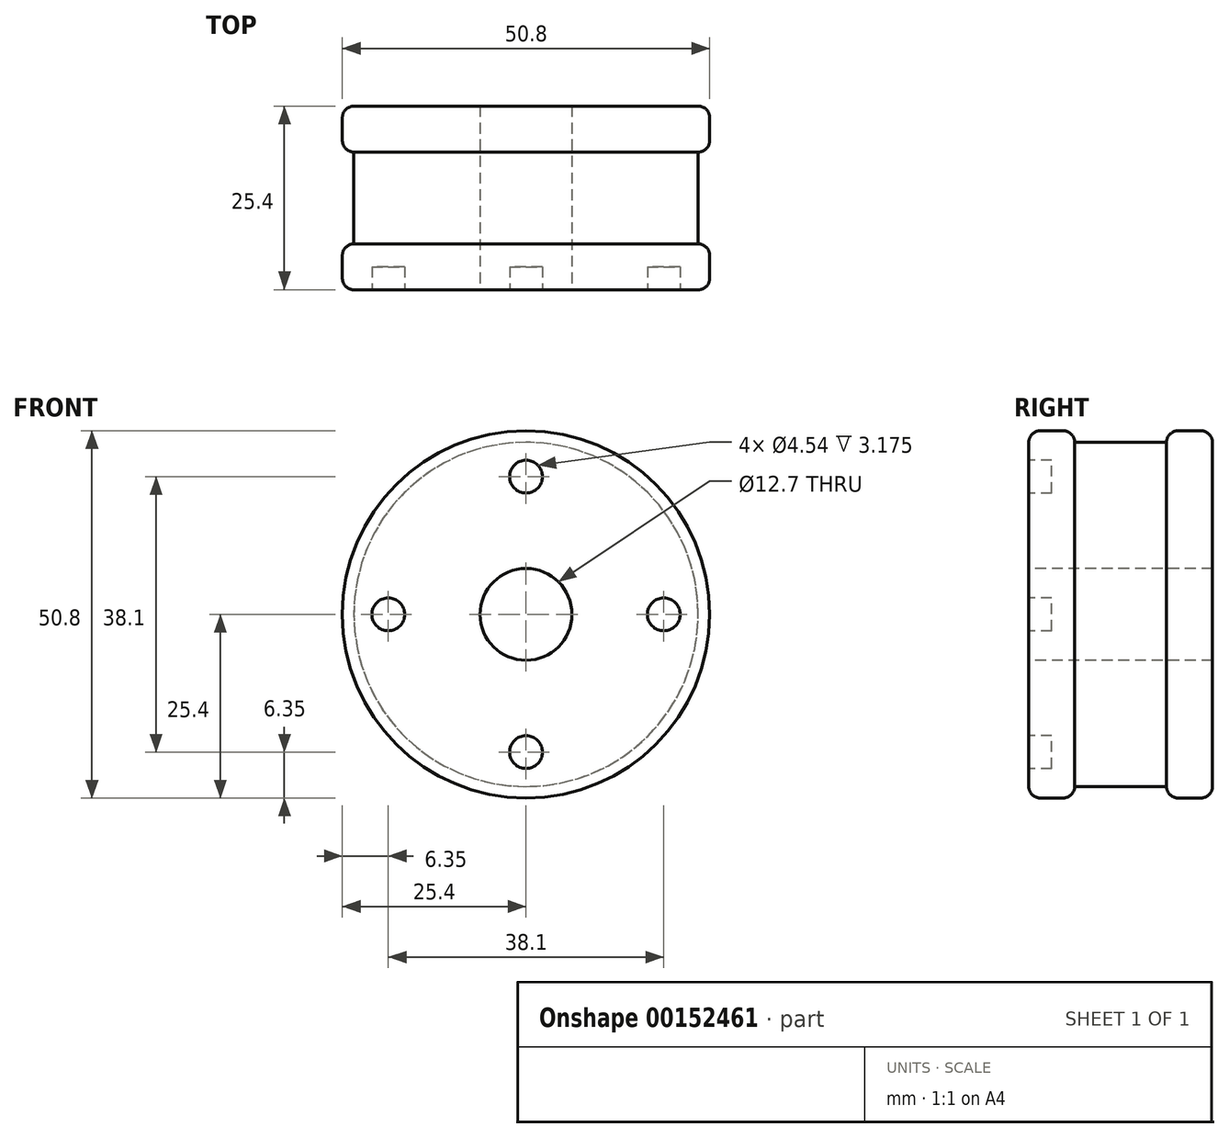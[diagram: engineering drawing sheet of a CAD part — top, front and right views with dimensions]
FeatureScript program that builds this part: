
annotation { "Feature Type Name" : "Feature", "Feature Type Description" : "" }
export const myFeature = defineFeature(function(context is Context, id is Id, definition is map)
    precondition{}
    {
        {
            var Q0;
            Q0=qCreatedBy(makeId("Front.planeOp"),FACE);
            var sketch = newSketch(context, id + "F0", { "sketchPlane" : qUnion([Q0])});
            skCircle(sketch, "E0", {"center": v(0, 0) * mm, "radius": 25.4 * mm});
            skSolve(sketch);
        }
        {
            var Q0;
            Q0 = qSketchRegion(id + "F0", true);
            extrude(context, id + "F1", {"entities" : qUnion([Q0]), "depth" : 6.35 * mm});
        }
        {
            var Q0;
            Q0=makeQuery(id+"F1.opExtrude","CAP_FACE",FACE,{"disambiguationData":[OSD([sQuery(id+"F0.wireOp",EDGE,"E0")])],"isStart":false});
            var sketch = newSketch(context, id + "F2", { "sketchPlane" : qUnion([Q0])});
            skCircle(sketch, "E1", {"center": v(0, 0) * mm, "radius": 23.81 * mm});
            skSolve(sketch);
        }
        {
            var Q0;
            Q0 = qSketchRegion(id + "F2", true);
            extrude(context, id + "F3", {"entities" : qUnion([Q0]), "operationType" : NewBodyOperationType.ADD, "depth" : 12.7 * mm});
        }
        {
            var Q0;
            Q0=makeQuery(id+"F3.opExtrude","CAP_FACE",FACE,{"disambiguationData":[OSD([sQuery(id+"F2.wireOp",EDGE,"E1")])],"isStart":false});
            var sketch = newSketch(context, id + "F4", { "sketchPlane" : qUnion([Q0])});
            skCircle(sketch, "E2", {"center": v(0, 0) * mm, "radius": 25.4 * mm});
            skSolve(sketch);
        }
        {
            var Q0;
            Q0 = qSketchRegion(id + "F4", true);
            extrude(context, id + "F5", {"entities" : qUnion([Q0]), "operationType" : NewBodyOperationType.ADD, "depth" : 6.35 * mm});
        }
        {
            var Q0;
            Q0=makeQuery(id+"F5.opExtrude","CAP_EDGE",EDGE,{"disambiguationData":[OSD([sQuery(id+"F4.wireOp",EDGE,"E2")])],"isStart":false});
            var Q1;
            Q1=makeQuery(id+"F5.opExtrude","CAP_EDGE",EDGE,{"disambiguationData":[OSD([sQuery(id+"F4.wireOp",EDGE,"E2")])],"isStart":true});
            var Q2;
            Q2=makeQuery(id+"F1.opExtrude","CAP_EDGE",EDGE,{"disambiguationData":[OSD([sQuery(id+"F0.wireOp",EDGE,"E0")])],"isStart":false});
            var Q3;
            Q3=makeQuery(id+"F1.opExtrude","CAP_EDGE",EDGE,{"disambiguationData":[OSD([sQuery(id+"F0.wireOp",EDGE,"E0")])],"isStart":true});
            fillet(context, id + "F6", {"entities" : qUnion([Q0, Q1, Q2, Q3]), "radius" : 1.6 * mm, "tangentPropagation" : true, "allowEdgeOverflow" : false});
        }
        {
            var Q0;
            Q0=makeQuery(id+"F5.opExtrude","CAP_FACE",FACE,{"disambiguationData":[OSD([sQuery(id+"F4.wireOp",EDGE,"E2")])],"isStart":false});
            var sketch = newSketch(context, id + "F7", { "sketchPlane" : qUnion([Q0])});
            skCircle(sketch, "E3", {"center": v(-19.05, 0) * mm, "radius": 2.27 * mm});
            skCircle(sketch, "E4.1.0", {"center": v(0, -19.05) * mm, "radius": 2.27 * mm});
            skCircle(sketch, "E4.2.0", {"center": v(19.05, 0) * mm, "radius": 2.27 * mm});
            skCircle(sketch, "E4.3.0", {"center": v(0, 19.05) * mm, "radius": 2.27 * mm});
            skPoint(sketch, "E4.center", {"position": v(0, 0) * mm});
            skSolve(sketch);
        }
        {
            var Q0;
            Q0 = qSketchRegion(id + "F7", true);
            extrude(context, id + "F8", {"entities" : qUnion([Q0]), "operationType" : NewBodyOperationType.REMOVE, "oppositeDirection" : true, "depth" : 3.17 * mm});
        }
        {
            var Q0;
            Q0=makeQuery(id+"F7.imprint","IMPRINT",FACE,{"disambiguationData":[TD([[makeQuery(id+"F7.imprint","IMPRINT",EDGE,{"derivedFrom":sQuery(id+"F7.wireOp",EDGE,"E3")}),-1.0]])]});
            var sketch = newSketch(context, id + "F9", { "sketchPlane" : qUnion([Q0])});
            skCircle(sketch, "E5", {"center": v(0, 0) * mm, "radius": 6.35 * mm});
            skSolve(sketch);
        }
        {
            var Q0;
            Q0 = qSketchRegion(id + "F9", true);
            extrude(context, id + "F10", {"entities" : qUnion([Q0]), "operationType" : NewBodyOperationType.REMOVE, "endBound" : BoundingType.THROUGH_ALL, "oppositeDirection" : true, "depth" : 25.4 * mm});
        }
    });
